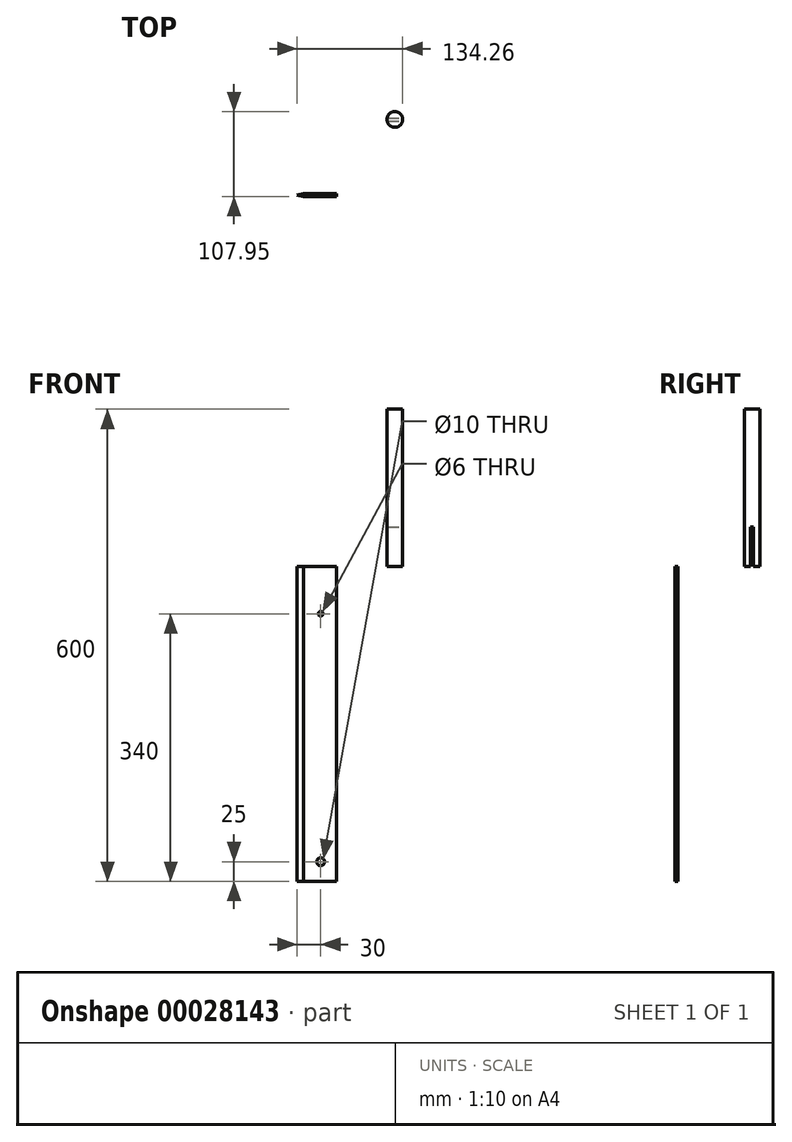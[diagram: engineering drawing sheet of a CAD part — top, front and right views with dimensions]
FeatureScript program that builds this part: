
annotation { "Feature Type Name" : "Feature", "Feature Type Description" : "" }
export const myFeature = defineFeature(function(context is Context, id is Id, definition is map)
    precondition{}
    {
        {
            var Q0;
            Q0=qCreatedBy(makeId("Front.planeOp"),FACE);
            var sketch = newSketch(context, id + "F0", { "sketchPlane" : qUnion([Q0])});
            skLineSegment(sketch, "E0.bottom", {"start": v(0, 0) * mm, "end": v(-50, 0) * mm});
            skLineSegment(sketch, "E0.top", {"start": v(0, -400) * mm, "end": v(-50, -400) * mm});
            skLineSegment(sketch, "E0.left", {"start": v(0, 0) * mm, "end": v(0, -400) * mm});
            skLineSegment(sketch, "E0.right", {"start": v(-50, 0) * mm, "end": v(-50, -400) * mm});
            skSolve(sketch);
        }
        {
            var Q0;
            Q0=makeQuery(id+"F0.imprint","IMPRINT",FACE,{"disambiguationData":[TD([[makeQuery(id+"F0.imprint","IMPRINT",EDGE,{"derivedFrom":sQuery(id+"F0.wireOp",EDGE,"E0.bottom")}),1.0]])]});
            extrude(context, id + "F1", {"entities" : qUnion([Q0]), "oppositeDirection" : true, "depth" : 4 * mm});
        }
        {
            var Q0;
            Q0=makeQuery(id+"F1.opExtrude","SWEPT_FACE",FACE,{"disambiguationData":[OSD([sQuery(id+"F0.wireOp",EDGE,"E0.bottom")])]});
            var sketch = newSketch(context, id + "F2", { "sketchPlane" : qUnion([Q0])});
            skLineSegment(sketch, "E1", {"start": v(-50, 2) * mm, "end": v(-42, 0) * mm});
            skLineSegment(sketch, "E2", {"start": v(-42, 0) * mm, "end": v(-42, 4) * mm});
            skLineSegment(sketch, "E3", {"start": v(-42, 4) * mm, "end": v(-50, 2) * mm});
            skSolve(sketch);
        }
        {
            var Q0;
            {var subQ2=sQuery(id+"F2.wireOp",EDGE,"E3");Q0=makeQuery(id+"F2.imprint","IMPRINT",FACE,{"disambiguationData":[TD([[makeQuery(id+"F2.imprint","IMPRINT",EDGE,{"derivedFrom":subQ2}),-1.0]])]});}
            var Q1;
            {var subQ2=sQuery(id+"F2.wireOp",EDGE,"E1");Q1=makeQuery(id+"F2.imprint","IMPRINT",FACE,{"disambiguationData":[TD([[makeQuery(id+"F2.imprint","IMPRINT",EDGE,{"derivedFrom":subQ2}),-1.0]])]});}
            extrude(context, id + "F3", {"entities" : qUnion([Q0, Q1]), "operationType" : NewBodyOperationType.REMOVE, "endBound" : BoundingType.UP_TO_NEXT, "oppositeDirection" : true, "depth" : 25 * mm});
        }
        {
            var Q0;
            Q0=makeQuery(id+"F1.opExtrude","CAP_FACE",FACE,{"disambiguationData":[OSD([sQuery(id+"F0.wireOp",EDGE,"E0.bottom"),sQuery(id+"F0.wireOp",EDGE,"E0.top"),sQuery(id+"F0.wireOp",EDGE,"E0.left"),sQuery(id+"F0.wireOp",EDGE,"E0.right")])],"isStart":false});
            var sketch = newSketch(context, id + "F4", { "sketchPlane" : qUnion([Q0])});
            skPoint(sketch, "E4", {"position": v(20, -375) * mm});
            skPoint(sketch, "E5", {"position": v(20, -60) * mm});
            skSolve(sketch);
        }
        {
            var Q0;
            Q0=sQuery(id+"F4.wireOp",VERTEX,"E4");
            var Q1;
            Q1=makeQuery(id+"F1.opExtrude","SWEPT_BODY",BODY,{"disambiguationData":[OSD([sQuery(id+"F0.wireOp",EDGE,"E0.bottom"),sQuery(id+"F0.wireOp",EDGE,"E0.top"),sQuery(id+"F0.wireOp",EDGE,"E0.left"),sQuery(id+"F0.wireOp",EDGE,"E0.right")])]});
            hole(context, id + "F5", {"style" : HoleStyle.SIMPLE, "holeDiameter" : 10 * mm, "endStyle" : HoleEndStyle.THROUGH, "locations" : qUnion([Q0]), "scope" : qUnion([Q1])});
        }
        {
            var Q0;
            Q0=sQuery(id+"F4.wireOp",VERTEX,"E5");
            var Q1;
            Q1=makeQuery(id+"F1.opExtrude","SWEPT_BODY",BODY,{"disambiguationData":[OSD([sQuery(id+"F0.wireOp",EDGE,"E0.bottom"),sQuery(id+"F0.wireOp",EDGE,"E0.top"),sQuery(id+"F0.wireOp",EDGE,"E0.left"),sQuery(id+"F0.wireOp",EDGE,"E0.right")])]});
            hole(context, id + "F6", {"style" : HoleStyle.SIMPLE, "holeDiameter" : 6 * mm, "endStyle" : HoleEndStyle.THROUGH, "locations" : qUnion([Q0]), "scope" : qUnion([Q1])});
        }
        {
            var Q0;
            Q0=qCreatedBy(makeId("Top.planeOp"),FACE);
            var sketch = newSketch(context, id + "F7", { "sketchPlane" : qUnion([Q0])});
            skCircle(sketch, "E6", {"center": v(74.26, 97.95) * mm, "radius": 10 * mm});
            skSolve(sketch);
        }
        {
            var Q0;
            Q0=makeQuery(id+"F7.imprint","IMPRINT",FACE,{"disambiguationData":[TD([[makeQuery(id+"F7.imprint","IMPRINT",EDGE,{"derivedFrom":sQuery(id+"F7.wireOp",EDGE,"E6")}),1.0]])]});
            extrude(context, id + "F8", {"entities" : qUnion([Q0]), "depth" : 200 * mm});
        }
        {
            var Q0;
            Q0=makeQuery(id+"F8.opExtrude","CAP_FACE",FACE,{"disambiguationData":[OSD([sQuery(id+"F7.wireOp",EDGE,"E6")])],"isStart":true});
            var sketch = newSketch(context, id + "F9", { "sketchPlane" : qUnion([Q0])});
            skLineSegment(sketch, "E7.rect.bottom", {"start": v(64.26, -99.95) * mm, "end": v(84.26, -99.95) * mm});
            skLineSegment(sketch, "E7.rect.top", {"start": v(64.26, -95.95) * mm, "end": v(84.26, -95.95) * mm});
            skLineSegment(sketch, "E7.rect.left", {"start": v(64.26, -99.95) * mm, "end": v(64.26, -95.95) * mm});
            skLineSegment(sketch, "E7.rect.right", {"start": v(84.26, -99.95) * mm, "end": v(84.26, -95.95) * mm});
            skPoint(sketch, "E7.rect.middle", {"position": v(74.26, -97.95) * mm});
            skSolve(sketch);
        }
        {
            var Q0;
            {var subQ0=makeQuery(id+"F8.opExtrude","CAP_EDGE",EDGE,{"disambiguationData":[OSD([sQuery(id+"F7.wireOp",EDGE,"E6")])],"isStart":true});var subQ6=sQuery(id+"F9.wireOp",EDGE,"E7.rect.bottom");var subQ8=makeQuery(id+"F9.imprint","INTERSECT",VERTEX,{"disambiguationData":[OD(0.0)],"derivedFrom":[subQ0,subQ6]});Q0=makeQuery(id+"F9.imprint","IMPRINT",FACE,{"disambiguationData":[TD([[makeQuery(id+"F9.imprint","IMPRINT",EDGE,{"disambiguationData":[TD([[subQ8,-1.0]])],"derivedFrom":subQ6}),1.0]])]});}
            extrude(context, id + "F10", {"entities" : qUnion([Q0]), "operationType" : NewBodyOperationType.REMOVE, "oppositeDirection" : true, "depth" : 50 * mm});
        }
    });
